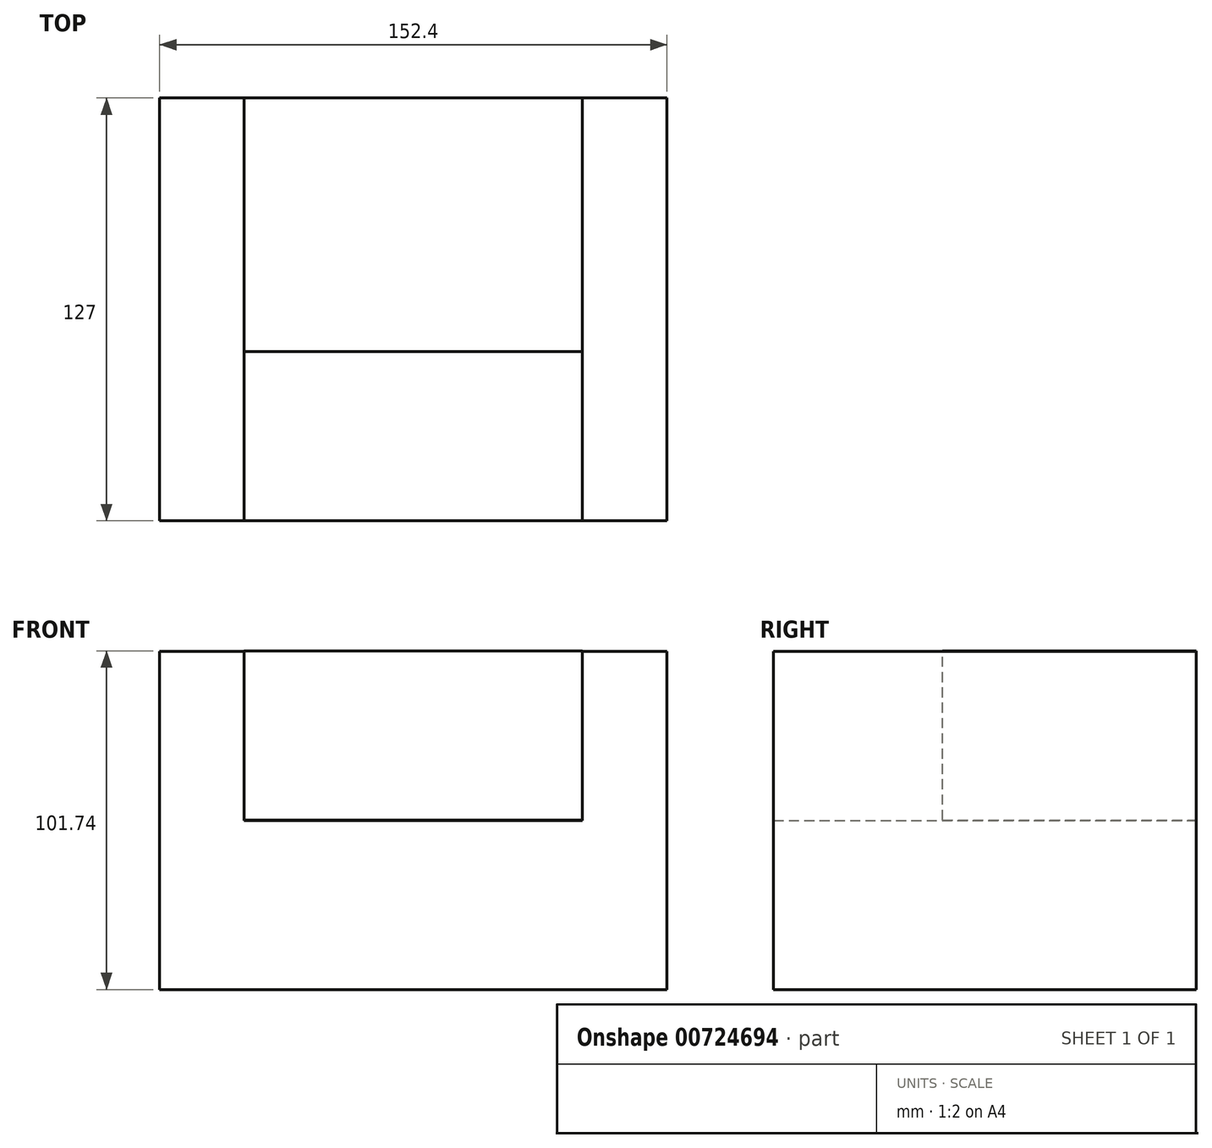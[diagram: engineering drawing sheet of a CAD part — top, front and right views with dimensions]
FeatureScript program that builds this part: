
annotation { "Feature Type Name" : "Feature", "Feature Type Description" : "" }
export const myFeature = defineFeature(function(context is Context, id is Id, definition is map)
    precondition{}
    {
        {
            var Q0;
            Q0=qCreatedBy(makeId("Front.planeOp"),FACE);
            var sketch = newSketch(context, id + "F0", { "sketchPlane" : qUnion([Q0])});
            skLineSegment(sketch, "E0", {"start": v(-25.4, -72.27) * mm, "end": v(127, -72.27) * mm});
            skLineSegment(sketch, "E1", {"start": v(127, -72.27) * mm, "end": v(127, 29.33) * mm});
            skLineSegment(sketch, "E2", {"start": v(127, 29.33) * mm, "end": v(101.6, 29.33) * mm});
            skLineSegment(sketch, "E3", {"start": v(101.6, 29.33) * mm, "end": v(101.6, -21.47) * mm});
            skLineSegment(sketch, "E4", {"start": v(101.6, -21.47) * mm, "end": v(0, -21.47) * mm});
            skLineSegment(sketch, "E5", {"start": v(0, -21.47) * mm, "end": v(0, 29.33) * mm});
            skLineSegment(sketch, "E6", {"start": v(0, 29.33) * mm, "end": v(-25.4, 29.33) * mm});
            skLineSegment(sketch, "E7", {"start": v(-25.4, 29.33) * mm, "end": v(-25.4, -72.27) * mm});
            skLineSegment(sketch, "E8", {"start": v(0, 29.33) * mm, "end": v(101.6, 29.33) * mm});
            skSolve(sketch);
        }
        {
            var Q0;
            Q0=makeQuery(id+"F0.imprint","IMPRINT",FACE,{"disambiguationData":[TD([[makeQuery(id+"F0.imprint","IMPRINT",EDGE,{"derivedFrom":sQuery(id+"F0.wireOp",EDGE,"E0")}),1.0]])]});
            extrude(context, id + "F1", {"entities" : qUnion([Q0]), "depth" : 127 * mm, "offsetDistance" : 25.4 * mm});
        }
        {
            var Q0;
            Q0=qCreatedBy(makeId("Front.planeOp"),FACE);
            var sketch = newSketch(context, id + "F2", { "sketchPlane" : qUnion([Q0])});
            skLineSegment(sketch, "E9", {"start": v(0, 29.47) * mm, "end": v(101.6, 29.47) * mm});
            skLineSegment(sketch, "E10", {"start": v(101.6, 29.47) * mm, "end": v(101.6, -21.33) * mm});
            skLineSegment(sketch, "E11", {"start": v(101.6, -21.33) * mm, "end": v(0, -21.33) * mm});
            skLineSegment(sketch, "E12", {"start": v(0, -21.33) * mm, "end": v(0, 29.47) * mm});
            skSolve(sketch);
        }
        {
            var Q0;
            Q0=makeQuery(id+"F2.imprint","IMPRINT",FACE,{"disambiguationData":[TD([[makeQuery(id+"F2.imprint","IMPRINT",EDGE,{"derivedFrom":sQuery(id+"F2.wireOp",EDGE,"E9")}),-1.0]])]});
            extrude(context, id + "F3", {"entities" : qUnion([Q0]), "operationType" : NewBodyOperationType.ADD, "depth" : 76.2 * mm, "offsetDistance" : 25.4 * mm});
        }
    });
